FCSTD DOCUMENT  (FreeCAD 0.14R3702 (Git))
Label: ballscrew_thread
License: CC-BY 3.0
LicenseURL: http://creativecommons.org/licenses/by/3.0/
objects: Sketcher::SketchObject×1, Part::Helix×1, Part::Sweep×1
note: 3 computed .brp shape members not serialized (recipe doc carries the construction recipe); baked Part::Feature solids carry a one-line shape summary decoded from their .brp

FEATURE [Sketcher::SketchObject] Sketch
  Placement = pos=(0,0,0) rot=(-1,0,0;4.71239rad)
  sketch-geometry (3):
    g0: ArcOfCircle CenterX=8 CenterY=-2.5 CenterZ=0 NormalX=0 NormalY=0 NormalZ=1 Radius=2 StartAngle=1.5708 EndAngle=4.71239
    g1: ArcOfCircle CenterX=8 CenterY=-0.25 CenterZ=0 NormalX=0 NormalY=0 NormalZ=1 Radius=0.25 StartAngle=4.71239 EndAngle=7.85398
    g2: ArcOfCircle CenterX=8 CenterY=-4.75 CenterZ=0 NormalX=0 NormalY=0 NormalZ=1 Radius=0.25 StartAngle=4.71239 EndAngle=7.85398
  constraints (6):
    c: PointOnObject(g1,g-1)
    c: Coincident(g0,g1)
    c: Coincident(g0,g2)
    c: DistanceY(g2,g1) = 5
    c: Radius(g1) = 0.25
    c: Radius(g2) = 0.25
FEATURE [Part::Helix] Helix
  Angle = 0
  Height = 750
  LocalCoord = 0
  Pitch = 5
  Radius = 8
  Style = 1
FEATURE [Part::Sweep] Sweep
  Frenet = true
  Sections = -> [Sketch]
  Solid = true
  Spine = -> Helix [Edge1]
  Transition = 1
